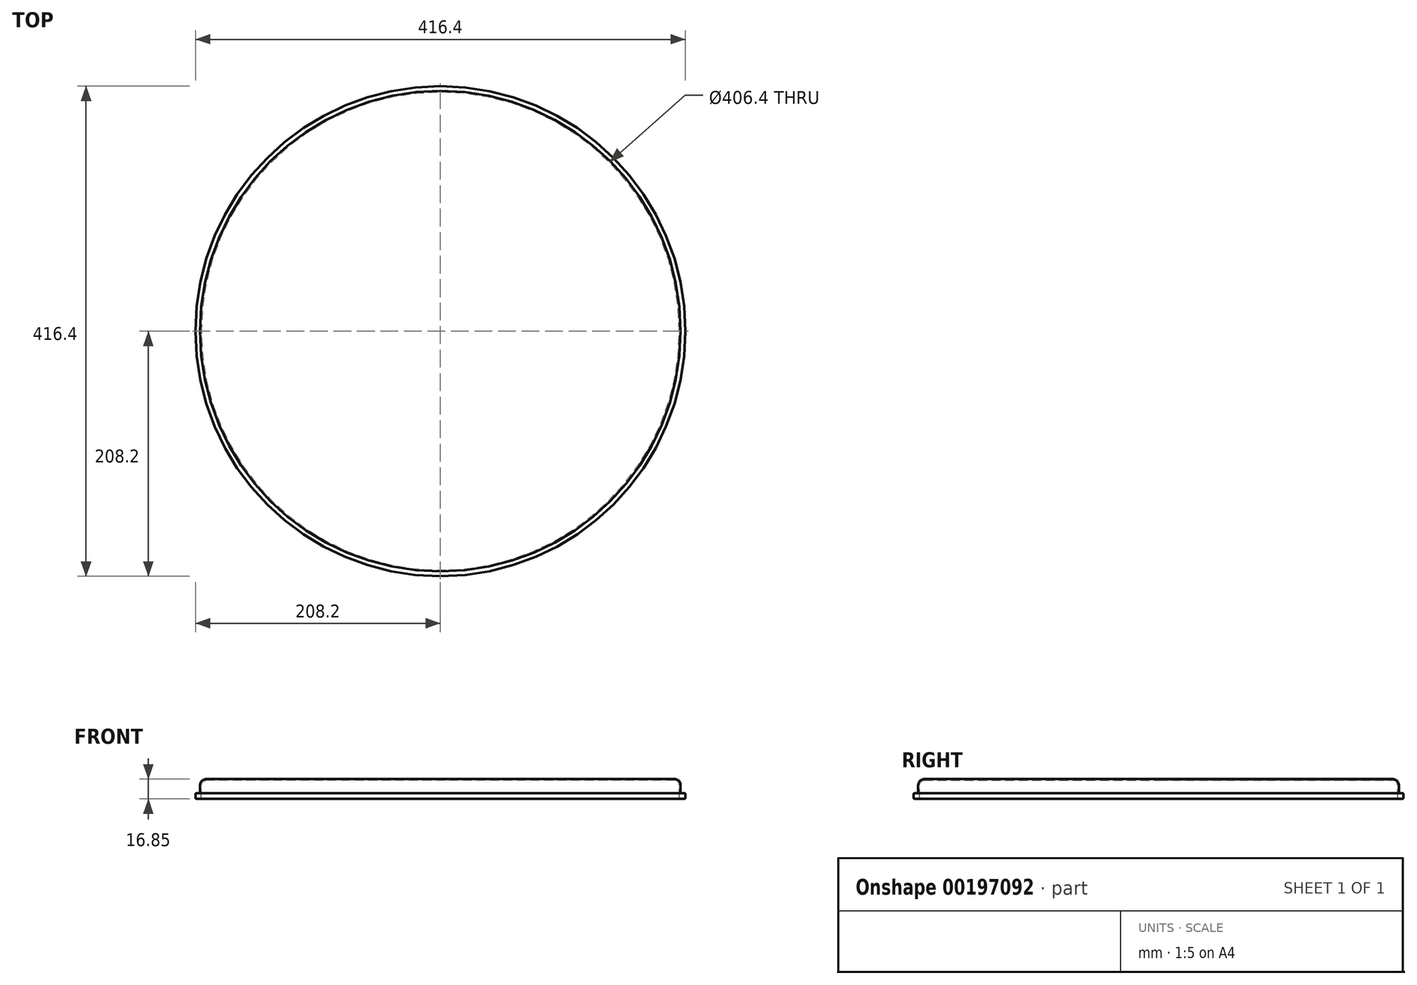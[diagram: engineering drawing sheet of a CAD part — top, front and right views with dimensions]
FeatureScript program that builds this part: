
annotation { "Feature Type Name" : "Feature", "Feature Type Description" : "" }
export const myFeature = defineFeature(function(context is Context, id is Id, definition is map)
    precondition{}
    {
        {
            var Q0;
            Q0=qCreatedBy(makeId("Front.planeOp"),FACE);
            var sketch = newSketch(context, id + "F0", { "sketchPlane" : qUnion([Q0])});
            skLineSegment(sketch, "E0", {"start": v(0, 0) * mm, "end": v(-199.2, 0) * mm});
            skLineSegment(sketch, "E1", {"start": v(-203.2, -4) * mm, "end": v(-203.2, -10.85) * mm});
            skArc(sketch, "E2", {"start": v(-199.2, 0) * mm, "mid": v(-202.03, -1.17) * mm, "end": v(-203.2, -4) * mm});
            skLineSegment(sketch, "E3", {"start": v(-203.2, -10.85) * mm, "end": v(-203.2, -14.85) * mm});
            skLineSegment(sketch, "E4", {"start": v(-204.2, -15.85) * mm, "end": v(-207.2, -15.85) * mm});
            skLineSegment(sketch, "E5", {"start": v(-208.2, -14.85) * mm, "end": v(-208.2, -11.85) * mm});
            skLineSegment(sketch, "E6", {"start": v(-207.2, -10.85) * mm, "end": v(-204.2, -10.85) * mm});
            skPoint(sketch, "E7.visualSharp", {"position": v(-208.2, -10.85) * mm});
            skArc(sketch, "E7.filletArc", {"start": v(-207.2, -10.85) * mm, "mid": v(-207.9, -11.14) * mm, "end": v(-208.2, -11.85) * mm});
            skPoint(sketch, "E8.visualSharp", {"position": v(-208.2, -15.85) * mm});
            skArc(sketch, "E8.filletArc", {"start": v(-208.2, -14.85) * mm, "mid": v(-207.9, -15.55) * mm, "end": v(-207.2, -15.85) * mm});
            skPoint(sketch, "E9.visualSharp", {"position": v(-203.2, -15.85) * mm});
            skArc(sketch, "E9.filletArc", {"start": v(-204.2, -15.85) * mm, "mid": v(-203.5, -15.55) * mm, "end": v(-203.2, -14.85) * mm});
            skLineSegment(sketch, "E10", {"start": v(-204.2, -10.85) * mm, "end": v(-204.2, -4) * mm});
            skArc(sketch, "E11.0", {"start": v(-199.2, 1) * mm, "mid": v(-202.74, -0.46) * mm, "end": v(-204.2, -4) * mm});
            skLineSegment(sketch, "E12", {"start": v(-199.2, 1) * mm, "end": v(0, 1) * mm});
            skLineSegment(sketch, "E13", {"start": v(0, 1) * mm, "end": v(0, 0) * mm});
            skSolve(sketch);
        }
        {
            var Q0;
            Q0=makeQuery(id+"F0.imprint","IMPRINT",FACE,{"disambiguationData":[TD([[makeQuery(id+"F0.imprint","IMPRINT",EDGE,{"derivedFrom":sQuery(id+"F0.wireOp",EDGE,"E0")}),-1.0]])]});
            var Q1;
            Q1=sQuery(id+"F0.wireOp",EDGE,"E13");
            revolve(context, id + "F1", {"entities" : qUnion([Q0]), "axis" : qUnion([Q1]), "revolveType" : RevolveType.FULL});
        }
    });
